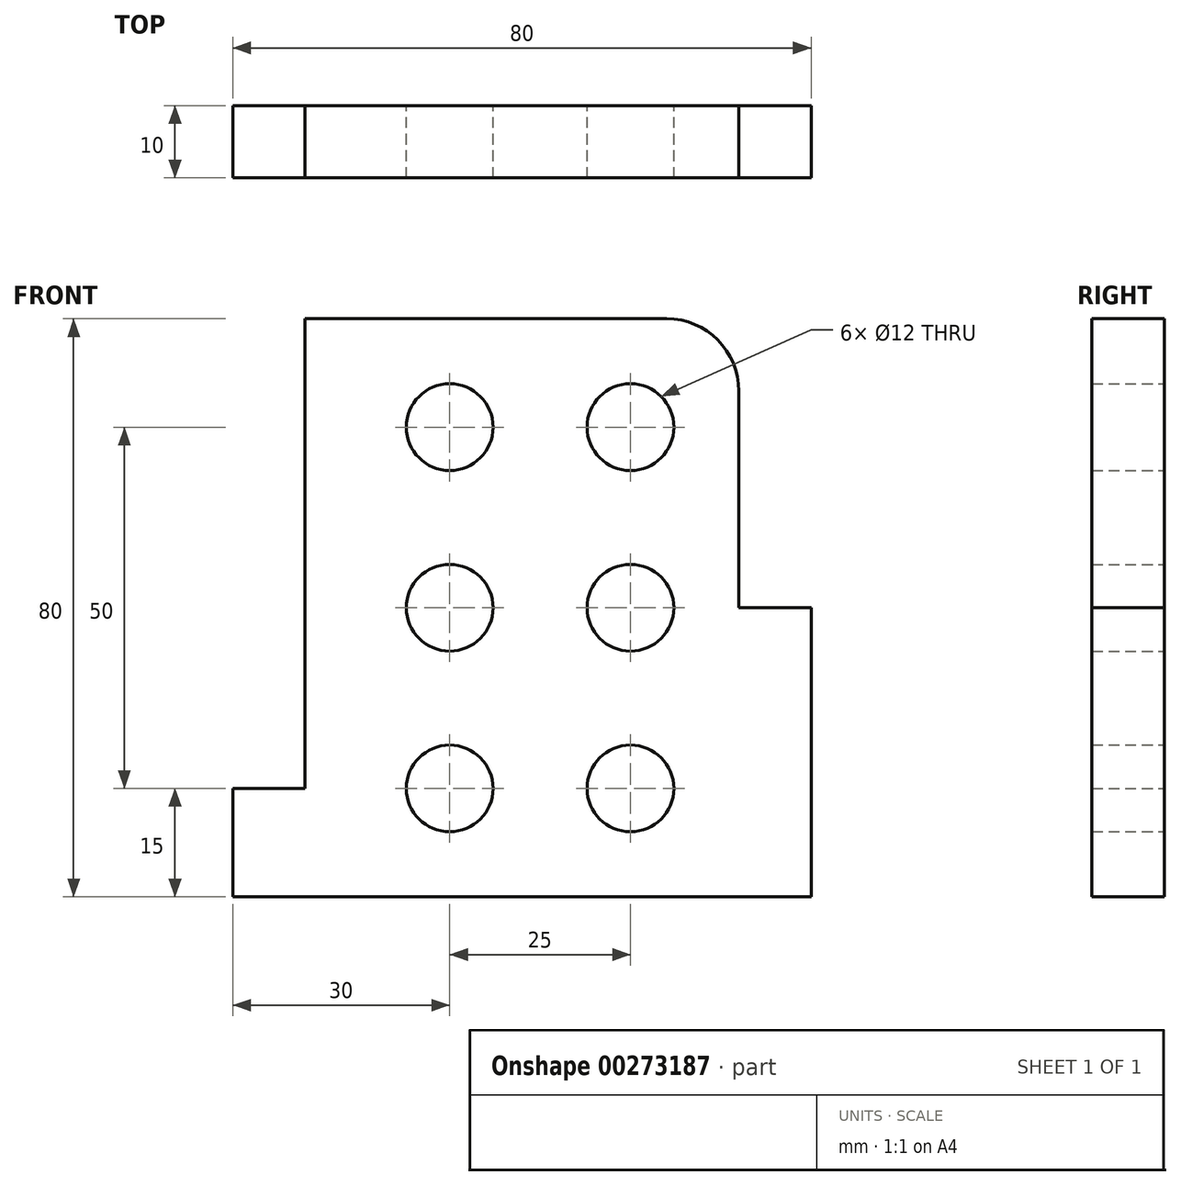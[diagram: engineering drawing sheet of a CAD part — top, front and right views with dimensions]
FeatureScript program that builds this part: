
annotation { "Feature Type Name" : "Feature", "Feature Type Description" : "" }
export const myFeature = defineFeature(function(context is Context, id is Id, definition is map)
    precondition{}
    {
        {
            var Q0;
            Q0=qCreatedBy(makeId("Front.planeOp"),FACE);
            var sketch = newSketch(context, id + "F0", { "sketchPlane" : qUnion([Q0])});
            skLineSegment(sketch, "E0", {"start": v(0, 0) * mm, "end": v(0, 15) * mm});
            skLineSegment(sketch, "E1", {"start": v(0, 15) * mm, "end": v(10, 15) * mm});
            skLineSegment(sketch, "E2", {"start": v(10, 15) * mm, "end": v(10, 80) * mm});
            skLineSegment(sketch, "E3", {"start": v(10, 80) * mm, "end": v(60, 80) * mm});
            skLineSegment(sketch, "E4", {"start": v(0, 0) * mm, "end": v(80, 0) * mm});
            skLineSegment(sketch, "E5", {"start": v(80, 0) * mm, "end": v(80, 40) * mm});
            skLineSegment(sketch, "E6", {"start": v(80, 40) * mm, "end": v(70, 40) * mm});
            skLineSegment(sketch, "E7", {"start": v(70, 40) * mm, "end": v(70, 70) * mm});
            skArc(sketch, "E8", {"start": v(70, 70) * mm, "mid": v(67.07, 77.07) * mm, "end": v(60, 80) * mm});
            skLineSegment(sketch, "E9", {"start": v(30, 65) * mm, "end": v(30, 15) * mm, "construction": true});
            skLineSegment(sketch, "E10", {"start": v(30, 15) * mm, "end": v(55, 15) * mm, "construction": true});
            skLineSegment(sketch, "E11", {"start": v(55, 15) * mm, "end": v(55, 65) * mm, "construction": true});
            skLineSegment(sketch, "E12", {"start": v(55, 65) * mm, "end": v(30, 65) * mm, "construction": true});
            skCircle(sketch, "E13", {"center": v(30, 65) * mm, "radius": 6 * mm});
            skCircle(sketch, "E14", {"center": v(55, 65) * mm, "radius": 6 * mm});
            skCircle(sketch, "E15", {"center": v(30, 40) * mm, "radius": 6 * mm});
            skCircle(sketch, "E16", {"center": v(55, 40) * mm, "radius": 6 * mm});
            skCircle(sketch, "E17", {"center": v(30, 15) * mm, "radius": 6 * mm});
            skCircle(sketch, "E18", {"center": v(55, 15) * mm, "radius": 6 * mm});
            skSolve(sketch);
        }
        {
            var Q0;
            Q0 = qSketchRegion(id + "F0", true);
            extrude(context, id + "F1", {"entities" : qUnion([Q0]), "depth" : 10 * mm});
        }
    });
